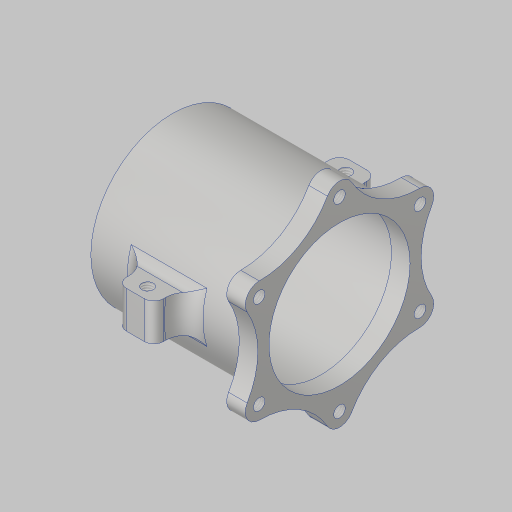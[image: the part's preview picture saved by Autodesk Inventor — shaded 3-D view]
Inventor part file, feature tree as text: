
AUTODESK INVENTOR PART (.ipt)
format: ipt  version: 2023.5 (Build 275446000, 446)  size: 283,136 bytes
history: native  units: in
note: dims shown in document units (in); Inventor stores cm internally (conversion verified against a paired STEP export)
features: sketch x6, extrude x4, projected_geometry x3, hole x2, fillet x2, plane x1, mirror x1
ambient origin geometry x8: Origin, YZ Plane, XZ Plane, XY Plane, X Axis, Y Axis, Z Axis, Center Point
bodies: Solid1 (feature_tree)
feature tree (19):
  extrude  "Extrusion1"  Depth=2.0in
  extrude  "Extrusion2"  Depth=2.0in
  hole  "Hole1"  [1 undecoded]
  plane  "Work Plane2"
  extrude  "Extrusion4"  Depth=1.0in
  mirror  "Mirror1"
  fillet  "Fillet1"  Radius=1.5in
  fillet  "Fillet2"  Radius=0.5in
  hole  "Hole2"  [1 undecoded]
  extrude  "Extrusion5"  Depth=0.25in
  sketch  "Sketch1"  dims[d0=2.0in d1=0.1in]
  sketch  "Sketch2"  dims[d2=2.0in d3=0.0in d4=3.0in]
  sketch  "Sketch3"  dims[d5=3.0in d6=0.25in d7=0.0in]
  sketch  "Sketch6"  dims[d9=2.3622in d11=360.0deg]
  sketch  "Sketch7"  dims[d13=0.156in d14=0.38in d15=0.375in d16=0.25in d17=0.5635in d18=1.0in d19=0.8108in d20=3.0in d22=1.5in d27=0.5in]
  sketch  "Sketch8"  dims[d28=0.5in d29=0.5in d30=0.0in d31=0.26in d32=0.13in d35=0.156in d36=0.38in d37=0.375in d38=0.25in d39=0.5635in d40=1.0in d41=0.8108in d42=1.9in d43=0.375in d44=0.25in d45=0.0in d46=2.5in d33=0.0in d34=0.0in]
  projected_geometry  "Project Cut Edges1"
  projected_geometry  "Project Cut Edges2"
  projected_geometry  "Project Cut Edges3"
note: 2 required parameter values undecoded (feature->parameter linkage not recoverable at this tier; creation-order binding heuristic only, values carry confidence <= 0.55)
